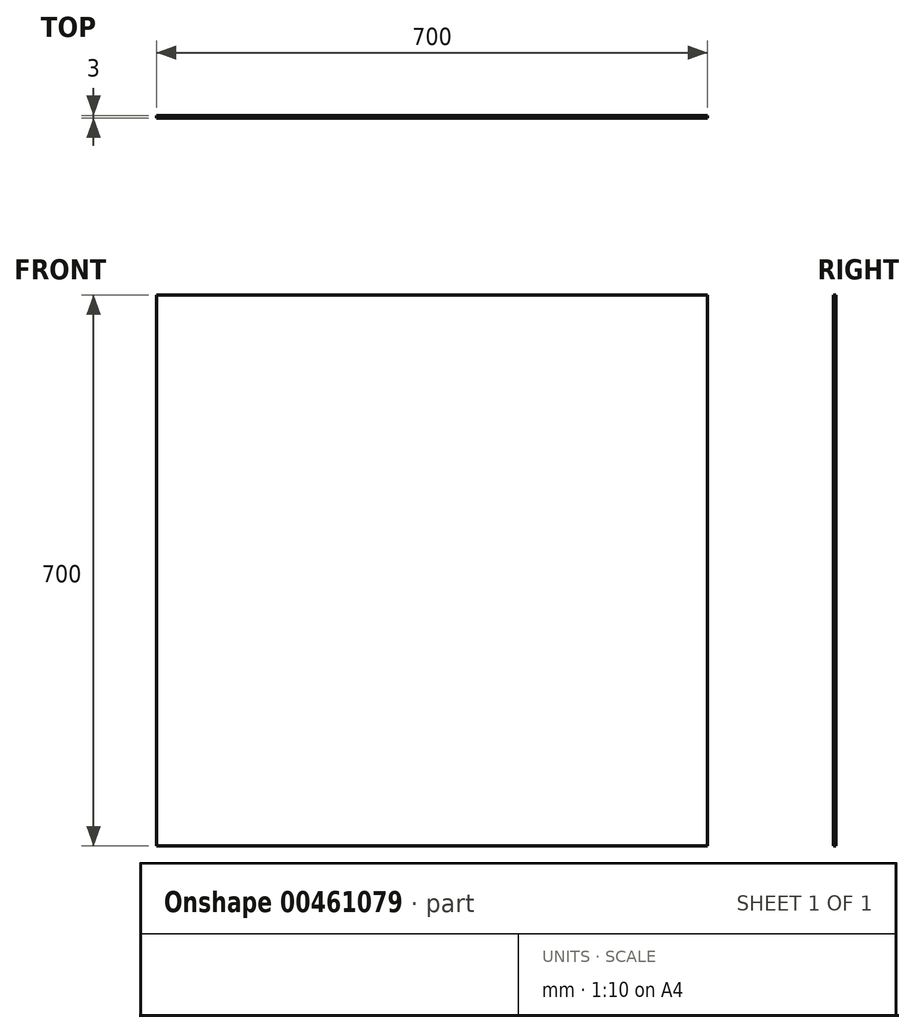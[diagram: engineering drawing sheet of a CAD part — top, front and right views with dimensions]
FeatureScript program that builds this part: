
annotation { "Feature Type Name" : "Feature", "Feature Type Description" : "" }
export const myFeature = defineFeature(function(context is Context, id is Id, definition is map)
    precondition{}
    {
        {
            var Q0;
            Q0=qCreatedBy(makeId("Front.planeOp"),FACE);
            var sketch = newSketch(context, id + "F0", { "sketchPlane" : qUnion([Q0])});
            skLineSegment(sketch, "E0.bottom", {"start": v(-731.3, 629.07) * mm, "end": v(-31.3, 629.07) * mm});
            skLineSegment(sketch, "E0.top", {"start": v(-731.3, -70.93) * mm, "end": v(-31.3, -70.93) * mm});
            skLineSegment(sketch, "E0.left", {"start": v(-731.3, 629.07) * mm, "end": v(-731.3, -70.93) * mm});
            skLineSegment(sketch, "E0.right", {"start": v(-31.3, 629.07) * mm, "end": v(-31.3, -70.93) * mm});
            skSolve(sketch);
        }
        {
            var Q0;
            Q0 = qSketchRegion(id + "F0", true);
            extrude(context, id + "F1", {"entities" : qUnion([Q0]), "depth" : 3 * mm});
        }
    });
